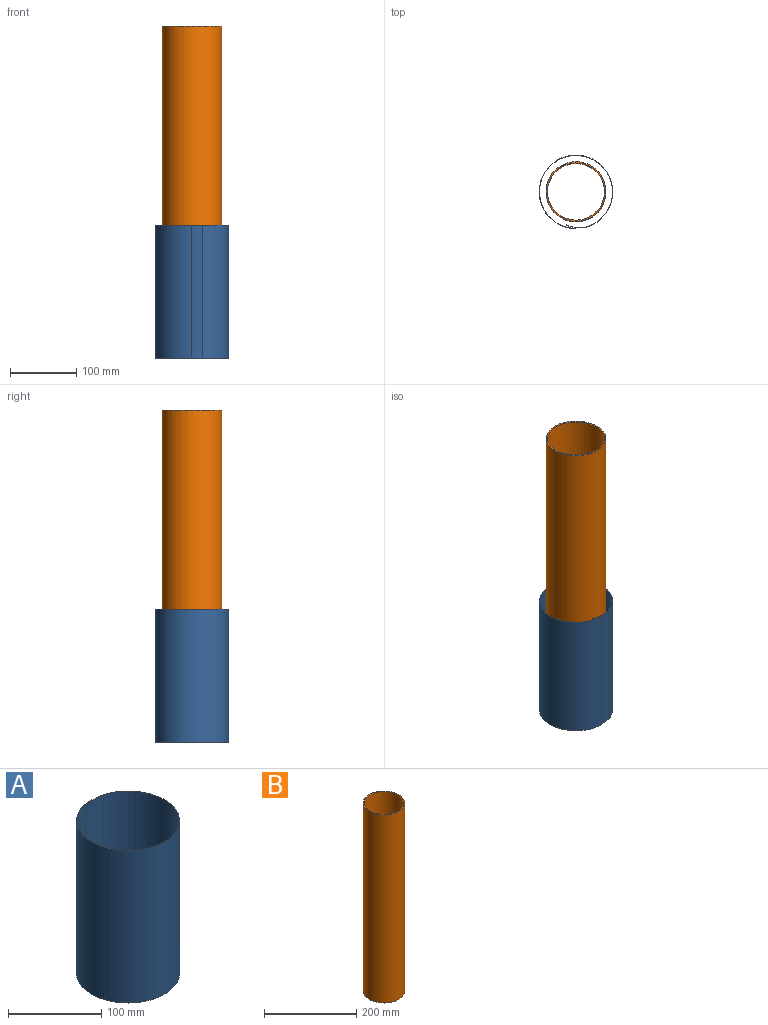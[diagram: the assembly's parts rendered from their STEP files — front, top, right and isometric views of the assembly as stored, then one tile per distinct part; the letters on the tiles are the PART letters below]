
ASSEMBLY  parts=2 mates=1
PART A: 8 faces, bbox 110.6x110.6x200 mm
  f0: plane 200x0.3mm, normal (1,0,0), area 60mm2, adj f1,f5,f6,f7
  f1: cylinder r=55.3mm len=200mm, axis (0,0,-1), area 66358.5mm2, adj f0,f2,f6,f7
  f2: cylinder r=55mm len=200mm, axis (0,0,-1), area 6148mm2, adj f1,f3,f6,f7
  f3: plane 200x0.28mm, normal (-0.93,-0.37,0), area 60mm2, adj f2,f4,f6,f7
  f4: cylinder r=54.7mm len=200mm, axis (0,0,-1), area 6111.3mm2, adj f3,f5,f6,f7
  f5: cylinder r=55mm len=200mm, axis (0,0,-1), area 65995.3mm2, adj f0,f4,f6,f7
  f6: plane 110.6x110.6mm, normal (0,0,1), area 108.5mm2, adj f0,f1,f2,f3,f4,f5
  f7: plane 110.6x110.6mm, normal (0,0,-1), area 108.5mm2, adj f0,f1,f2,f3,f4,f5
PART B: 4 faces, bbox 90x90x500 mm
  f0: cylinder r=43mm len=500mm, axis (0,0,-1), area 135088.5mm2, adj f2,f3
  f1: cylinder r=45mm len=500mm, axis (0,0,-1), area 141371.7mm2, adj f2,f3
  f2: plane 90x90mm, normal (0,0,-1), area 552.9mm2, adj f0,f1
  f3: plane 90x90mm, normal (0,0,1), area 552.9mm2, adj f0,f1
PLACE A rot(axis=(1,0,0),180deg) t=(-99.09,103.91,138.29)mm
PLACE B t=(-99.09,103.91,-61.71)mm
MATE fastened A.f5 <-> B.f0  axis (0,0,1) through (-99.09,103.91,138.29)mm
